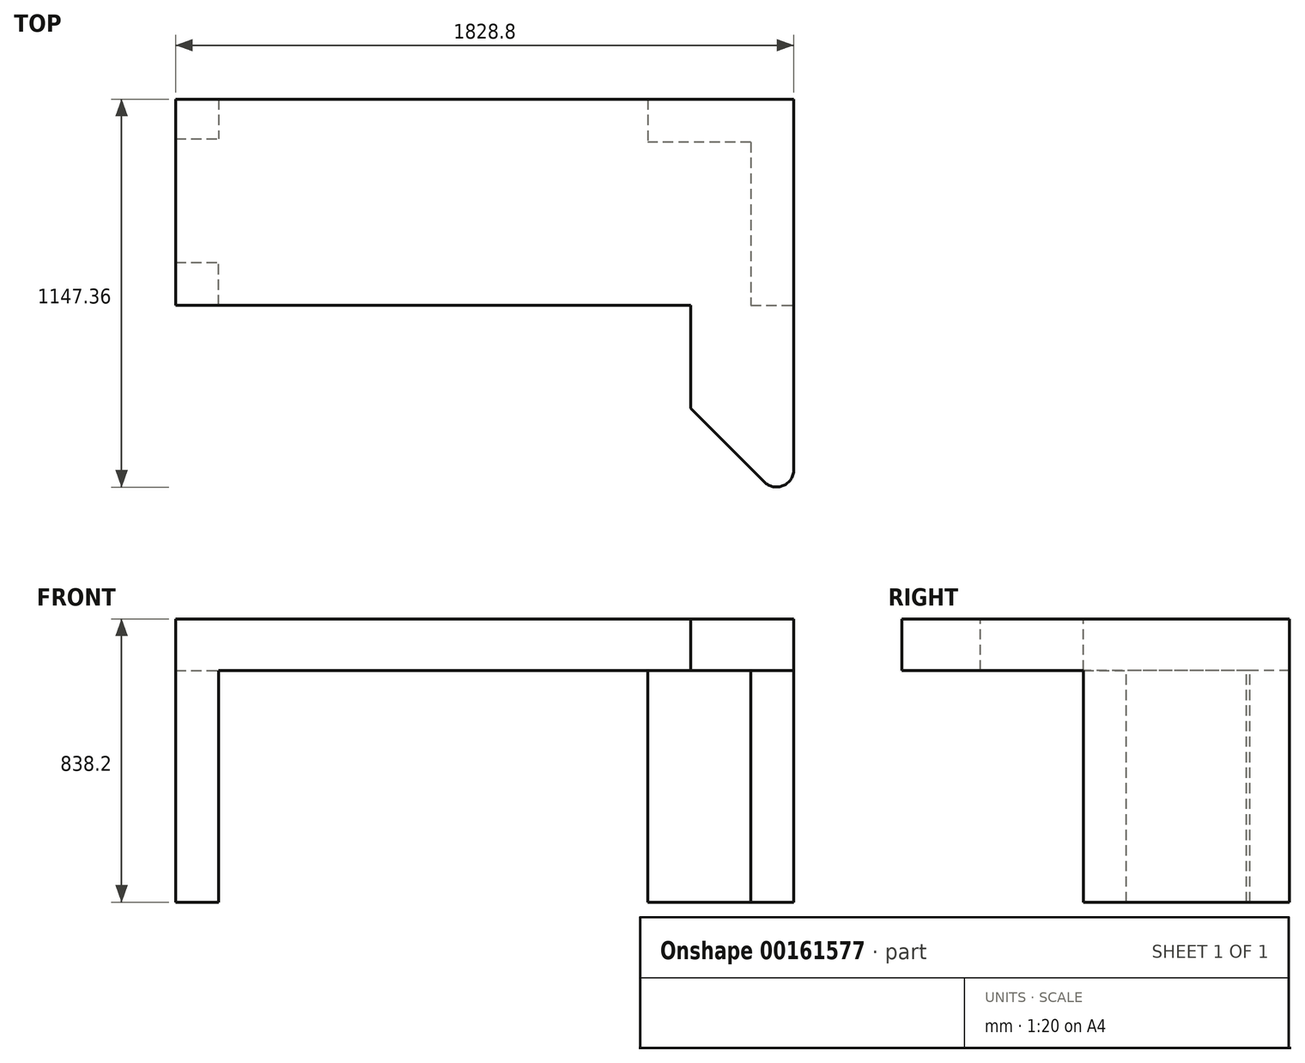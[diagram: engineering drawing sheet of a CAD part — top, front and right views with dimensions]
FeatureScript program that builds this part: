
annotation { "Feature Type Name" : "Feature", "Feature Type Description" : "" }
export const myFeature = defineFeature(function(context is Context, id is Id, definition is map)
    precondition{}
    {
        {
            var Q0;
            Q0=qCreatedBy(makeId("Top.planeOp"),FACE);
            var sketch = newSketch(context, id + "F0", { "sketchPlane" : qUnion([Q0])});
            skLineSegment(sketch, "E0.bottom", {"start": v(914.4, 304.8) * mm, "end": v(-914.4, 304.8) * mm});
            skLineSegment(sketch, "E0.top", {"start": v(914.4, -304.8) * mm, "end": v(-914.4, -304.8) * mm});
            skLineSegment(sketch, "E0.left", {"start": v(914.4, 304.8) * mm, "end": v(914.4, -304.8) * mm});
            skLineSegment(sketch, "E0.right", {"start": v(-914.4, 304.8) * mm, "end": v(-914.4, -304.8) * mm});
            skPoint(sketch, "E0.middle", {"position": v(0, 0) * mm});
            skSolve(sketch);
        }
        {
            var Q0;
            Q0 = qSketchRegion(id + "F0", true);
            extrude(context, id + "F1", {"entities" : qUnion([Q0]), "depth" : 152.4 * mm});
        }
        {
            var Q0;
            Q0=makeQuery(id+"F1.opExtrude","CAP_FACE",FACE,{"disambiguationData":[OSD([sQuery(id+"F0.wireOp",EDGE,"E0.bottom"),sQuery(id+"F0.wireOp",EDGE,"E0.top"),sQuery(id+"F0.wireOp",EDGE,"E0.left"),sQuery(id+"F0.wireOp",EDGE,"E0.right")])],"isStart":true});
            var sketch = newSketch(context, id + "F2", { "sketchPlane" : qUnion([Q0])});
            skLineSegment(sketch, "E1.bottom", {"start": v(-914.4, 304.8) * mm, "end": v(-787.4, 304.8) * mm});
            skLineSegment(sketch, "E1.top", {"start": v(-914.4, 177.8) * mm, "end": v(-787.4, 177.8) * mm});
            skLineSegment(sketch, "E1.left", {"start": v(-914.4, 304.8) * mm, "end": v(-914.4, 177.8) * mm});
            skLineSegment(sketch, "E1.right", {"start": v(-787.4, 304.8) * mm, "end": v(-787.4, 177.8) * mm});
            skLineSegment(sketch, "E2.bottom", {"start": v(-914.4, -304.8) * mm, "end": v(-787.4, -304.8) * mm});
            skLineSegment(sketch, "E2.top", {"start": v(-914.4, -187.88) * mm, "end": v(-787.4, -187.88) * mm});
            skLineSegment(sketch, "E2.left", {"start": v(-914.4, -304.8) * mm, "end": v(-914.4, -187.88) * mm});
            skLineSegment(sketch, "E2.right", {"start": v(-787.4, -304.8) * mm, "end": v(-787.4, -187.88) * mm});
            skLineSegment(sketch, "E3.bottom", {"start": v(914.4, -304.8) * mm, "end": v(787.4, -304.8) * mm});
            skLineSegment(sketch, "E3.left", {"start": v(914.4, -304.8) * mm, "end": v(914.4, 177.8) * mm});
            skLineSegment(sketch, "E4.left", {"start": v(914.4, 304.8) * mm, "end": v(914.4, 177.8) * mm});
            skLineSegment(sketch, "E5.bottom", {"start": v(787.4, -304.8) * mm, "end": v(482.6, -304.8) * mm});
            skLineSegment(sketch, "E5.top", {"start": v(787.4, -177.8) * mm, "end": v(482.6, -177.8) * mm});
            skLineSegment(sketch, "E5.right", {"start": v(482.6, -304.8) * mm, "end": v(482.6, -177.8) * mm});
            skLineSegment(sketch, "E6", {"start": v(787.4, -177.8) * mm, "end": v(787.4, 304.8) * mm});
            skLineSegment(sketch, "E7", {"start": v(787.4, 304.8) * mm, "end": v(914.4, 304.8) * mm});
            skSolve(sketch);
        }
        {
            var Q0;
            Q0 = qSketchRegion(id + "F2", true);
            extrude(context, id + "F3", {"entities" : qUnion([Q0]), "operationType" : NewBodyOperationType.ADD, "depth" : 685.8 * mm});
        }
        {
            var Q0;
            Q0=makeQuery(id+"F1.opExtrude","CAP_FACE",FACE,{"disambiguationData":[OSD([sQuery(id+"F0.wireOp",EDGE,"E0.bottom"),sQuery(id+"F0.wireOp",EDGE,"E0.top"),sQuery(id+"F0.wireOp",EDGE,"E0.left"),sQuery(id+"F0.wireOp",EDGE,"E0.right")])],"isStart":false});
            var sketch = newSketch(context, id + "F4", { "sketchPlane" : qUnion([Q0])});
            skLineSegment(sketch, "E8.bottom", {"start": v(914.4, -304.8) * mm, "end": v(609.6, -304.8) * mm});
            skLineSegment(sketch, "E8.left", {"start": v(914.4, -304.8) * mm, "end": v(914.4, -791.76) * mm});
            skLineSegment(sketch, "E9", {"start": v(609.6, -609.6) * mm, "end": v(827.68, -827.68) * mm});
            skPoint(sketch, "E10.visualSharp", {"position": v(914.4, -914.4) * mm});
            skArc(sketch, "E10.filletArc", {"start": v(827.68, -827.68) * mm, "mid": v(883.04, -838.7) * mm, "end": v(914.4, -791.76) * mm});
            skLineSegment(sketch, "E11", {"start": v(609.6, -304.8) * mm, "end": v(609.6, -609.6) * mm});
            skSolve(sketch);
        }
        {
            var Q0;
            Q0 = qSketchRegion(id + "F4", true);
            var Q1;
            Q1=makeQuery(id+"F1.opExtrude","CAP_FACE",FACE,{"disambiguationData":[OSD([sQuery(id+"F0.wireOp",EDGE,"E0.bottom"),sQuery(id+"F0.wireOp",EDGE,"E0.top"),sQuery(id+"F0.wireOp",EDGE,"E0.left"),sQuery(id+"F0.wireOp",EDGE,"E0.right")])],"isStart":true});
            extrude(context, id + "F5", {"entities" : qUnion([Q0]), "operationType" : NewBodyOperationType.ADD, "endBound" : BoundingType.UP_TO_SURFACE, "oppositeDirection" : true, "endBoundEntityFace" : qUnion([Q1]), "depth" : 152.4 * mm});
        }
    });
